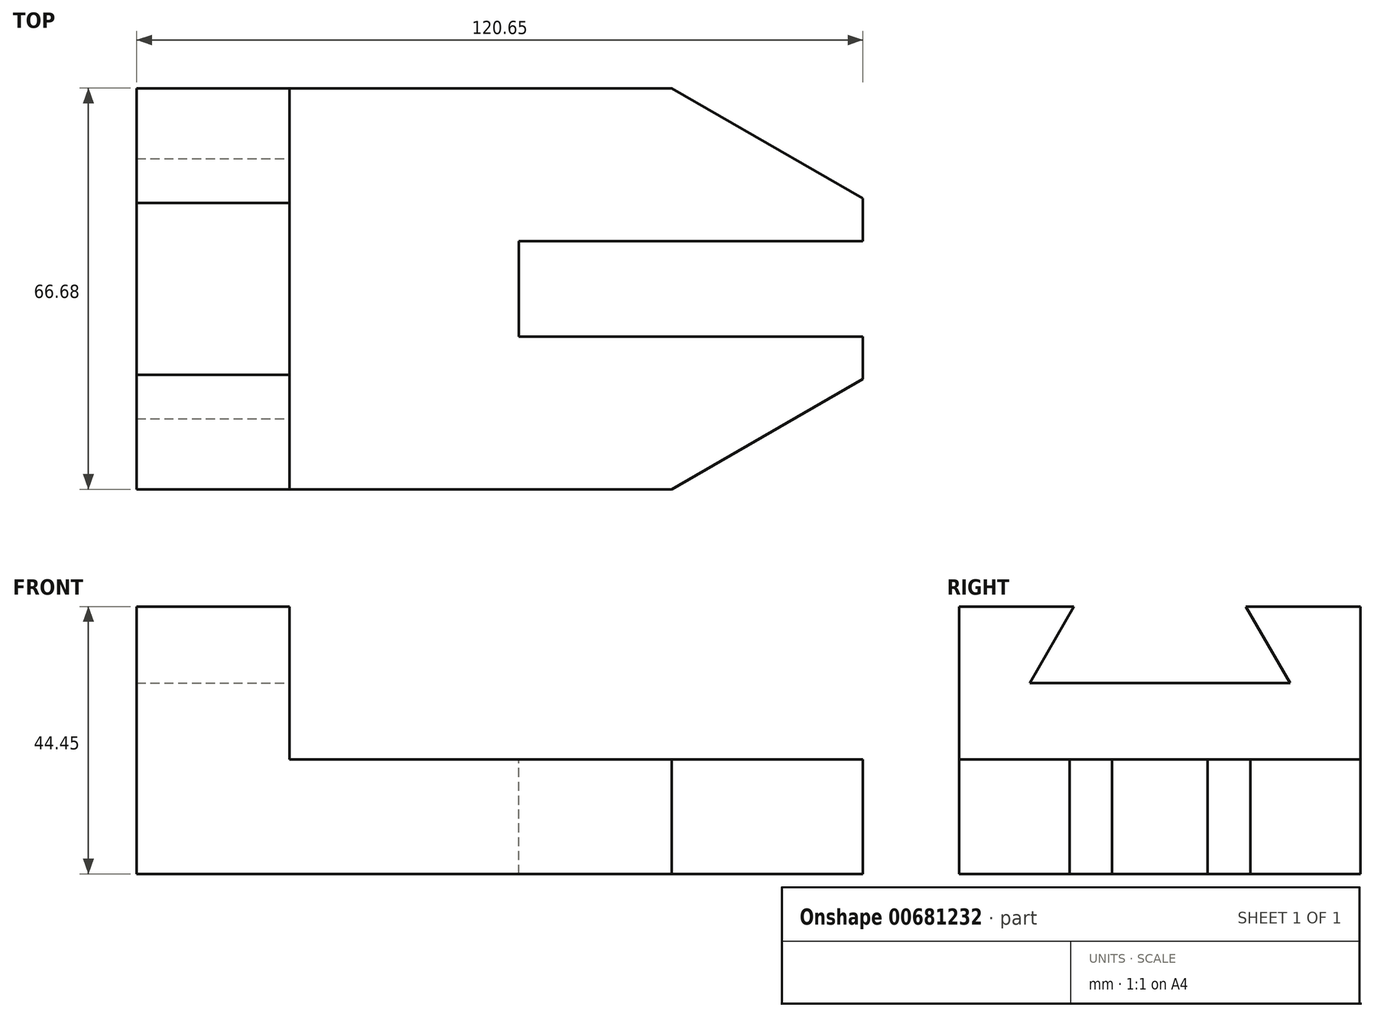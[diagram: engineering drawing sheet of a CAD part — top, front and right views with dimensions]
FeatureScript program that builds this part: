
annotation { "Feature Type Name" : "Feature", "Feature Type Description" : "" }
export const myFeature = defineFeature(function(context is Context, id is Id, definition is map)
    precondition{}
    {
        {
            var Q0;
            Q0=qCreatedBy(makeId("Front.planeOp"),FACE);
            var sketch = newSketch(context, id + "F0", { "sketchPlane" : qUnion([Q0])});
            skLineSegment(sketch, "E0.bottom", {"start": v(-64.61, 9.93) * mm, "end": v(56.04, 9.93) * mm});
            skLineSegment(sketch, "E0.top", {"start": v(-64.61, -34.52) * mm, "end": v(56.04, -34.52) * mm});
            skLineSegment(sketch, "E0.left", {"start": v(-64.61, 9.93) * mm, "end": v(-64.61, -34.52) * mm});
            skLineSegment(sketch, "E0.right", {"start": v(56.04, 9.93) * mm, "end": v(56.04, -34.52) * mm});
            skSolve(sketch);
        }
        {
            var Q0;
            Q0=makeQuery(id+"F0.imprint","IMPRINT",FACE,{"disambiguationData":[TD([[makeQuery(id+"F0.imprint","IMPRINT",EDGE,{"derivedFrom":sQuery(id+"F0.wireOp",EDGE,"E0.bottom")}),-1.0]])]});
            extrude(context, id + "F1", {"entities" : qUnion([Q0]), "oppositeDirection" : true, "depth" : 66.67 * mm, "offsetDistance" : 25.4 * mm});
        }
        {
            var Q0;
            Q0=makeQuery(id+"F1.opExtrude","CAP_FACE",FACE,{"disambiguationData":[OSD([sQuery(id+"F0.wireOp",EDGE,"E0.bottom"),sQuery(id+"F0.wireOp",EDGE,"E0.top"),sQuery(id+"F0.wireOp",EDGE,"E0.left"),sQuery(id+"F0.wireOp",EDGE,"E0.right")])],"isStart":true});
            var sketch = newSketch(context, id + "F2", { "sketchPlane" : qUnion([Q0])});
            skLineSegment(sketch, "E1.bottom", {"start": v(56.04, 9.93) * mm, "end": v(-39.21, 9.93) * mm});
            skLineSegment(sketch, "E1.top", {"start": v(56.04, -15.47) * mm, "end": v(-39.21, -15.47) * mm});
            skLineSegment(sketch, "E1.left", {"start": v(56.04, 9.93) * mm, "end": v(56.04, -15.47) * mm});
            skLineSegment(sketch, "E1.right", {"start": v(-39.21, 9.93) * mm, "end": v(-39.21, -15.47) * mm});
            skSolve(sketch);
        }
        {
            var Q0;
            Q0=makeQuery(id+"F2.imprint","IMPRINT",FACE,{"disambiguationData":[TD([[makeQuery(id+"F2.imprint","IMPRINT",EDGE,{"derivedFrom":sQuery(id+"F2.wireOp",EDGE,"E1.bottom")}),-1.0]])]});
            extrude(context, id + "F3", {"entities" : qUnion([Q0]), "operationType" : NewBodyOperationType.REMOVE, "endBound" : BoundingType.THROUGH_ALL, "oppositeDirection" : true, "depth" : 25.4 * mm, "offsetDistance" : 25.4 * mm});
        }
        {
            var Q0;
            Q0=makeQuery(id+"F3.boolean.opBoolean","COPY",FACE,{"derivedFrom":makeQuery(id+"F3.opExtrude","SWEPT_FACE",FACE,{"disambiguationData":[OSD([sQuery(id+"F2.wireOp",EDGE,"E1.top")])]})});
            var sketch = newSketch(context, id + "F4", { "sketchPlane" : qUnion([Q0])});
            skLineSegment(sketch, "E2.bottom", {"start": v(56.04, 41.27) * mm, "end": v(-1.11, 41.27) * mm});
            skLineSegment(sketch, "E2.top", {"start": v(56.04, 25.4) * mm, "end": v(-1.11, 25.4) * mm});
            skLineSegment(sketch, "E2.left", {"start": v(56.04, 41.28) * mm, "end": v(56.04, 25.4) * mm});
            skLineSegment(sketch, "E2.right", {"start": v(-1.11, 41.27) * mm, "end": v(-1.11, 25.4) * mm});
            skSolve(sketch);
        }
        {
            var Q0;
            Q0=makeQuery(id+"F4.imprint","IMPRINT",FACE,{"disambiguationData":[TD([[makeQuery(id+"F4.imprint","IMPRINT",EDGE,{"derivedFrom":sQuery(id+"F4.wireOp",EDGE,"E2.bottom")}),1.0]])]});
            extrude(context, id + "F5", {"entities" : qUnion([Q0]), "operationType" : NewBodyOperationType.REMOVE, "endBound" : BoundingType.THROUGH_ALL, "oppositeDirection" : true, "depth" : 25.4 * mm, "offsetDistance" : 25.4 * mm});
        }
        {
            var Q0;
            Q0=makeQuery(id+"F3.boolean.opBoolean","COPY",FACE,{"derivedFrom":makeQuery(id+"F3.opExtrude","SWEPT_FACE",FACE,{"disambiguationData":[OSD([sQuery(id+"F2.wireOp",EDGE,"E1.top")])]})});
            var sketch = newSketch(context, id + "F6", { "sketchPlane" : qUnion([Q0])});
            skLineSegment(sketch, "E3", {"start": v(56.04, 18.33) * mm, "end": v(24.29, 0) * mm});
            skLineSegment(sketch, "E4", {"start": v(56.04, 48.34) * mm, "end": v(24.29, 66.67) * mm});
            skSolve(sketch);
        }
        {
            var Q0;
            {var subQ0=sQuery(id+"F6.wireOp",EDGE,"E4");Q0=makeQuery(id+"F6.imprint","IMPRINT",FACE,{"disambiguationData":[TD([[makeQuery(id+"F6.imprint","IMPRINT",EDGE,{"derivedFrom":subQ0}),-1.0]])]});}
            var Q1;
            {var subQ0=sQuery(id+"F6.wireOp",EDGE,"E3");Q1=makeQuery(id+"F6.imprint","IMPRINT",FACE,{"disambiguationData":[TD([[makeQuery(id+"F6.imprint","IMPRINT",EDGE,{"derivedFrom":subQ0}),1.0]])]});}
            extrude(context, id + "F7", {"entities" : qUnion([Q0, Q1]), "operationType" : NewBodyOperationType.REMOVE, "endBound" : BoundingType.THROUGH_ALL, "oppositeDirection" : true, "depth" : 25.4 * mm, "offsetDistance" : 25.4 * mm});
        }
        {
            var Q0;
            Q0=makeQuery(id+"F3.boolean.opBoolean","COPY",FACE,{"derivedFrom":makeQuery(id+"F3.opExtrude","SWEPT_FACE",FACE,{"disambiguationData":[OSD([sQuery(id+"F2.wireOp",EDGE,"E1.right")])]})});
            var sketch = newSketch(context, id + "F8", { "sketchPlane" : qUnion([Q0])});
            skLineSegment(sketch, "E5", {"start": v(11.72, -2.77) * mm, "end": v(54.96, -2.77) * mm});
            skLineSegment(sketch, "E6", {"start": v(54.96, -2.77) * mm, "end": v(47.63, 9.93) * mm});
            skLineSegment(sketch, "E7", {"start": v(11.72, -2.77) * mm, "end": v(19.05, 9.93) * mm});
            skSolve(sketch);
        }
        {
            var Q0;
            Q0=makeQuery(id+"F8.imprint","IMPRINT",FACE,{"disambiguationData":[TD([[makeQuery(id+"F8.imprint","IMPRINT",EDGE,{"derivedFrom":sQuery(id+"F8.wireOp",EDGE,"E5")}),1.0]])]});
            extrude(context, id + "F9", {"entities" : qUnion([Q0]), "operationType" : NewBodyOperationType.REMOVE, "endBound" : BoundingType.THROUGH_ALL, "oppositeDirection" : true, "depth" : 25.4 * mm, "offsetDistance" : 25.4 * mm});
        }
    });
